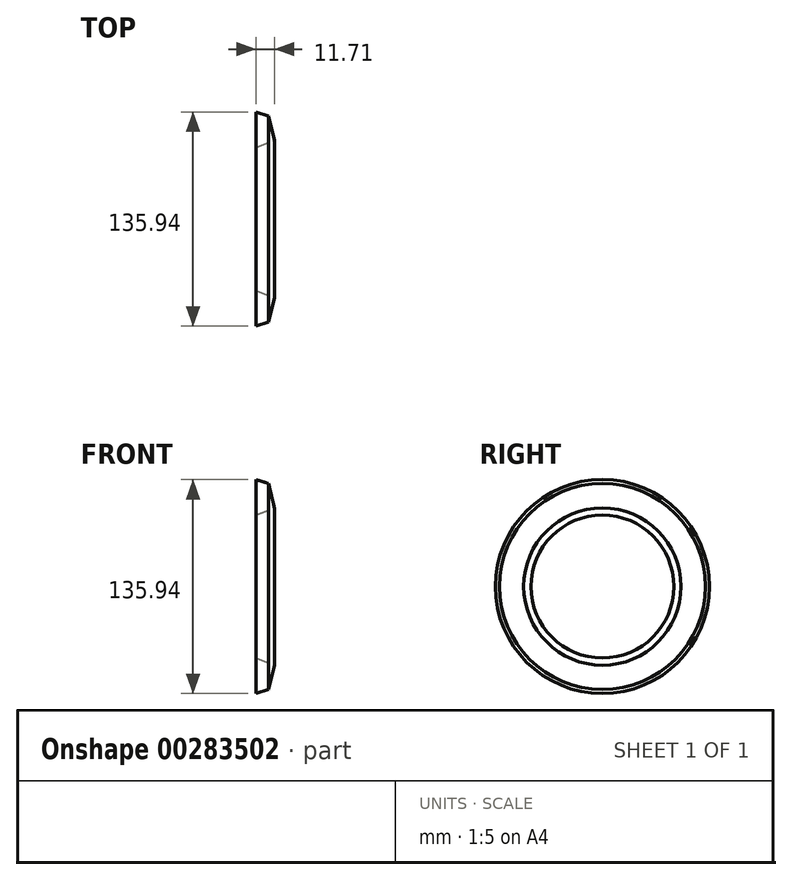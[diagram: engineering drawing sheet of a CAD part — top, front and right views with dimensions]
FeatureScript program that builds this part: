
annotation { "Feature Type Name" : "Feature", "Feature Type Description" : "" }
export const myFeature = defineFeature(function(context is Context, id is Id, definition is map)
    precondition{}
    {
        {
            var Q0;
            Q0=qCreatedBy(makeId("Front.planeOp"),FACE);
            var sketch = newSketch(context, id + "F0", { "sketchPlane" : qUnion([Q0])});
            skLineSegment(sketch, "E0", {"start": v(0, 67.97) * mm, "end": v(0, 45.4) * mm});
            skLineSegment(sketch, "E1", {"start": v(0, 45.4) * mm, "end": v(11.7, 49.98) * mm});
            skLineSegment(sketch, "E2", {"start": v(11.7, 49.98) * mm, "end": v(8, 65.4) * mm});
            skLineSegment(sketch, "E3", {"start": v(8, 65.4) * mm, "end": v(0, 67.97) * mm});
            skLineSegment(sketch, "E4", {"start": v(0, 0) * mm, "end": v(33.41, 0) * mm});
            skSolve(sketch);
        }
        {
            var Q0;
            Q0=makeQuery(id+"F0.imprint","IMPRINT",FACE,{"disambiguationData":[TD([[makeQuery(id+"F0.imprint","IMPRINT",EDGE,{"derivedFrom":sQuery(id+"F0.wireOp",EDGE,"E0")}),1.0]])]});
            var Q1;
            Q1=sQuery(id+"F0.wireOp",EDGE,"E4");
            revolve(context, id + "F1", {"entities" : qUnion([Q0]), "axis" : qUnion([Q1]), "revolveType" : RevolveType.FULL});
        }
    });
